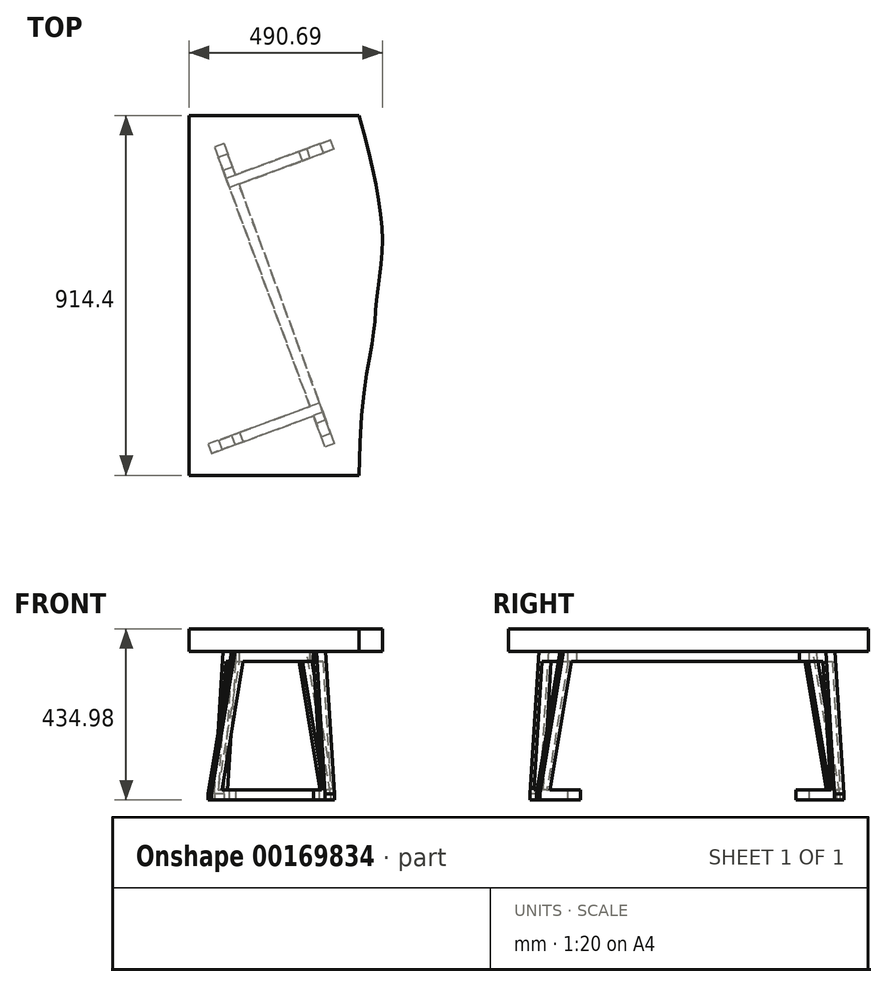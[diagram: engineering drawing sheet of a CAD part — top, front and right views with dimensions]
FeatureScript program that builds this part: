
annotation { "Feature Type Name" : "Feature", "Feature Type Description" : "" }
export const myFeature = defineFeature(function(context is Context, id is Id, definition is map)
    precondition{}
    {
        {
            var Q0;
            Q0=qCreatedBy(makeId("Top.planeOp"),FACE);
            var sketch = newSketch(context, id + "F0", { "sketchPlane" : qUnion([Q0])});
            skLineSegment(sketch, "E0", {"start": v(0, 0) * mm, "end": v(-431.8, 0) * mm});
            skLineSegment(sketch, "E1", {"start": v(-431.8, 0) * mm, "end": v(-431.8, 914.4) * mm});
            skLineSegment(sketch, "E2", {"start": v(-431.8, 914.4) * mm, "end": v(0, 914.4) * mm});
            skFitSpline(sketch, "E3", {"points": [v(0, 914.4) * mm, v(51.21, 686.94) * mm, v(57.73, 557.59) * mm, v(44.27, 444.48) * mm, v(35.04, 350.61) * mm, v(0, 0) * mm], "startDerivative": vector(304.49, -1066.3) * mm, "endDerivative": vector(0, -2055.33) * mm});
            skSolve(sketch);
        }
        {
            var Q0;
            Q0=qSketchRegion(id+"F0",true);
            extrude(context, id + "F1", {"entities" : qUnion([Q0]), "depth" : 57.15 * mm});
        }
        {
            var Q0;
            Q0=makeQuery(id+"F1.opExtrude","CAP_FACE",FACE,{"disambiguationData":[OSD([sQuery(id+"F0.wireOp",EDGE,"E0"),sQuery(id+"F0.wireOp",EDGE,"E1"),sQuery(id+"F0.wireOp",EDGE,"E2"),sQuery(id+"F0.wireOp",EDGE,"E3")])],"isStart":true});
            var sketch = newSketch(context, id + "F2", { "sketchPlane" : qUnion([Q0])});
            skLineSegment(sketch, "E4", {"start": v(-74.81, -838.2) * mm, "end": v(-355.6, -734.73) * mm});
            skLineSegment(sketch, "E5", {"start": v(-355.6, -76.2) * mm, "end": v(-74.81, -179.67) * mm});
            skLineSegment(sketch, "E6", {"start": v(-355.6, -76.2) * mm, "end": v(-355.6, -734.73) * mm});
            skLineSegment(sketch, "E7", {"start": v(-355.6, -76.2) * mm, "end": v(-355.6, 0) * mm, "construction": true});
            skLineSegment(sketch, "E8", {"start": v(-74.81, -838.2) * mm, "end": v(-74.81, -914.4) * mm, "construction": true});
            skLineSegment(sketch, "E9.bottom", {"start": v(-355.6, -76.2) * mm, "end": v(-74.81, -76.2) * mm});
            skLineSegment(sketch, "E9.top", {"start": v(-355.6, -838.2) * mm, "end": v(-74.81, -838.2) * mm});
            skLineSegment(sketch, "E9.left", {"start": v(-355.6, -76.2) * mm, "end": v(-355.6, -838.2) * mm});
            skLineSegment(sketch, "E9.right", {"start": v(-74.81, -76.2) * mm, "end": v(-74.81, -838.2) * mm});
            skLineSegment(sketch, "E10", {"start": v(-355.6, -76.2) * mm, "end": v(-431.8, -76.2) * mm, "construction": true});
            skLineSegment(sketch, "E11", {"start": v(0, 0) * mm, "end": v(0, -914.4) * mm, "construction": true});
            skLineSegment(sketch, "E12", {"start": v(-74.81, -76.2) * mm, "end": v(1.39, -76.2) * mm, "construction": true});
            skLineSegment(sketch, "E13", {"start": v(-74.81, -76.2) * mm, "end": v(-355.6, -838.2) * mm});
            skPoint(sketch, "E14", {"position": v(-108.38, -167.3) * mm});
            skPoint(sketch, "E15", {"position": v(-322.03, -747.1) * mm});
            skSolve(sketch);
        }
        {
            var Q0;
            Q0=makeQuery(id+"F1.opExtrude","SWEPT_FACE",FACE,{"disambiguationData":[OSD([sQuery(id+"F0.wireOp",EDGE,"E0")])]});
            var Q1;
            Q1=sQuery(id+"F2.wireOp",VERTEX,"E9.right.start");
            cPlane(context, id + "F3", {"entities" : qUnion([Q0, Q1]), "cplaneType" : CPlaneType.PLANE_POINT, "offset" : 25.4 * mm, "width" : 152.4 * mm, "height" : 152.4 * mm});
        }
        {
            var Q0;
            Q0=qCreatedBy(id+"F3.planeOp",FACE);
            var sketch = newSketch(context, id + "F4", { "sketchPlane" : qUnion([Q0])});
            skLineSegment(sketch, "E16", {"start": v(-74.81, 0) * mm, "end": v(-74.81, -361.95) * mm});
            skSolve(sketch);
        }
        {
            var Q0;
            Q0=sQuery(id+"F4.wireOp",VERTEX,"E16.end");
            var Q1;
            Q1=sQuery(id+"F4.wireOp",VERTEX,"E16.start");
            var Q2;
            Q2=sQuery(id+"F2.wireOp",VERTEX,"E9.left.end");
            cPlane(context, id + "F5", {"entities" : qUnion([Q0, Q1, Q2]), "cplaneType" : CPlaneType.THREE_POINT, "offset" : 25.4 * mm, "width" : 152.4 * mm, "height" : 152.4 * mm});
        }
        {
            var Q0;
            Q0=qCreatedBy(id+"F5.planeOp",FACE);
            var sketch = newSketch(context, id + "F6", { "sketchPlane" : qUnion([Q0])});
            skLineSegment(sketch, "E17", {"start": v(97.37, -361.95) * mm, "end": v(161.19, 0) * mm});
            skLineSegment(sketch, "E18", {"start": v(161.19, 0) * mm, "end": v(503.41, 0) * mm});
            skLineSegment(sketch, "E19", {"start": v(503.41, 0) * mm, "end": v(503.41, -361.95) * mm, "construction": true});
            skLineSegment(sketch, "E20", {"start": v(97.37, -361.95) * mm, "end": v(161.19, -361.95) * mm, "construction": true});
            skLineSegment(sketch, "E21", {"start": v(161.19, -361.95) * mm, "end": v(161.19, 0) * mm, "construction": true});
            skLineSegment(sketch, "E22", {"start": v(503.41, -25.4) * mm, "end": v(182.5, -25.4) * mm});
            skLineSegment(sketch, "E23", {"start": v(182.5, -25.4) * mm, "end": v(124.84, -352.43) * mm});
            skLineSegment(sketch, "E24", {"start": v(97.37, -361.95) * mm, "end": v(97.37, -377.82) * mm});
            skLineSegment(sketch, "E25", {"start": v(97.37, -377.82) * mm, "end": v(207.15, -377.82) * mm});
            skLineSegment(sketch, "E26", {"start": v(207.15, -377.82) * mm, "end": v(207.15, -352.43) * mm});
            skLineSegment(sketch, "E27", {"start": v(124.84, -352.43) * mm, "end": v(207.15, -352.43) * mm});
            skLineSegment(sketch, "E28", {"start": v(503.41, -25.4) * mm, "end": v(503.41, 0) * mm});
            skLineSegment(sketch, "E29.MirrorCS", {"start": v(503.41, -25.4) * mm, "end": v(824.32, -25.4) * mm});
            skLineSegment(sketch, "E30.MirrorCS", {"start": v(824.32, -25.4) * mm, "end": v(881.98, -352.43) * mm});
            skLineSegment(sketch, "E31.MirrorCS", {"start": v(845.63, 0) * mm, "end": v(503.41, 0) * mm});
            skLineSegment(sketch, "E32.MirrorCS", {"start": v(909.45, -361.95) * mm, "end": v(845.63, 0) * mm});
            skLineSegment(sketch, "E33.MirrorCS", {"start": v(881.98, -352.43) * mm, "end": v(799.67, -352.43) * mm});
            skLineSegment(sketch, "E34.MirrorCS", {"start": v(799.67, -377.82) * mm, "end": v(799.67, -352.43) * mm});
            skLineSegment(sketch, "E35.MirrorCS", {"start": v(909.45, -377.82) * mm, "end": v(799.67, -377.82) * mm});
            skLineSegment(sketch, "E36.MirrorCS", {"start": v(909.45, -361.95) * mm, "end": v(909.45, -377.82) * mm});
            skSolve(sketch);
        }
        {
            var Q0;
            Q0 = qSketchRegion(id + "F6", true);
            extrude(context, id + "F7", {"entities" : qUnion([Q0]), "operationType" : NewBodyOperationType.ADD, "endBound" : BoundingType.SYMMETRIC, "depth" : 25.4 * mm, "offsetDistance" : 25.4 * mm});
        }
        {
            var Q0;
            Q0=makeQuery(id+"F7.opExtrude","SWEPT_FACE",FACE,{"disambiguationData":[OSD([sQuery(id+"F6.wireOp",EDGE,"E26")])]});
            var Q1;
            Q1=sQuery(id+"F2.wireOp",VERTEX,"E14");
            cPlane(context, id + "F8", {"entities" : qUnion([Q0, Q1]), "cplaneType" : CPlaneType.PLANE_POINT, "offset" : 25.4 * mm, "width" : 152.4 * mm, "height" : 152.4 * mm});
        }
        {
            var Q0;
            Q0=qCreatedBy(id+"F8.planeOp",FACE);
            var sketch = newSketch(context, id + "F9", { "sketchPlane" : qUnion([Q0])});
            skLineSegment(sketch, "E37", {"start": v(56.55, 0) * mm, "end": v(268.57, 0) * mm});
            skLineSegment(sketch, "E38", {"start": v(268.57, 0) * mm, "end": v(332.4, -361.95) * mm});
            skLineSegment(sketch, "E39", {"start": v(332.4, -361.95) * mm, "end": v(332.4, -377.82) * mm});
            skLineSegment(sketch, "E40", {"start": v(332.4, -377.82) * mm, "end": v(56.55, -377.82) * mm});
            skLineSegment(sketch, "E41", {"start": v(56.55, -377.82) * mm, "end": v(56.55, -352.43) * mm});
            skLineSegment(sketch, "E42", {"start": v(56.55, -352.43) * mm, "end": v(304.92, -352.43) * mm});
            skLineSegment(sketch, "E43", {"start": v(304.92, -352.43) * mm, "end": v(247.26, -25.4) * mm});
            skLineSegment(sketch, "E44", {"start": v(247.26, -25.4) * mm, "end": v(56.55, -25.4) * mm});
            skLineSegment(sketch, "E45", {"start": v(56.55, -25.4) * mm, "end": v(56.55, 0) * mm});
            skLineSegment(sketch, "E46", {"start": v(388.57, 0) * mm, "end": v(388.57, -300.75) * mm, "construction": true});
            skSolve(sketch);
        }
        {
            var Q0;
            Q0 = qSketchRegion(id + "F9", true);
            extrude(context, id + "F10", {"entities" : qUnion([Q0]), "operationType" : NewBodyOperationType.ADD, "endBound" : BoundingType.SYMMETRIC, "depth" : 25.4 * mm, "offsetDistance" : 25.4 * mm});
        }
        {
            var Q0;
            Q0=makeQuery(id+"F7.opExtrude","SWEPT_FACE",FACE,{"disambiguationData":[OSD([sQuery(id+"F6.wireOp",EDGE,"E34.MirrorCS")])]});
            cPlane(context, id + "F11", {"entities" : qUnion([Q0]), "cplaneType" : CPlaneType.OFFSET, "offset" : 12.7 * mm, "oppositeDirection" : true, "width" : 152.4 * mm, "height" : 152.4 * mm});
        }
        {
            var Q0;
            Q0=qCreatedBy(id+"F11.planeOp",FACE);
            var sketch = newSketch(context, id + "F12", { "sketchPlane" : qUnion([Q0])});
            skLineSegment(sketch, "E47", {"start": v(-31.15, -377.82) * mm, "end": v(226.07, -377.82) * mm});
            skLineSegment(sketch, "E48", {"start": v(226.07, -361.95) * mm, "end": v(162.25, 0) * mm});
            skLineSegment(sketch, "E49", {"start": v(162.25, 0) * mm, "end": v(-31.15, 0) * mm});
            skLineSegment(sketch, "E50", {"start": v(-31.15, 0) * mm, "end": v(-31.15, -25.4) * mm});
            skLineSegment(sketch, "E51", {"start": v(-31.15, -25.4) * mm, "end": v(140.94, -25.4) * mm});
            skLineSegment(sketch, "E52", {"start": v(140.94, -25.4) * mm, "end": v(198.6, -352.43) * mm});
            skLineSegment(sketch, "E53", {"start": v(198.6, -352.43) * mm, "end": v(-31.15, -352.43) * mm});
            skLineSegment(sketch, "E54", {"start": v(-31.15, -352.43) * mm, "end": v(-31.15, -377.82) * mm});
            skLineSegment(sketch, "E55", {"start": v(226.07, -361.95) * mm, "end": v(226.07, -377.82) * mm});
            skSolve(sketch);
        }
        {
            var Q0;
            Q0 = qSketchRegion(id + "F12", true);
            extrude(context, id + "F13", {"entities" : qUnion([Q0]), "operationType" : NewBodyOperationType.ADD, "endBound" : BoundingType.SYMMETRIC, "depth" : 25.4 * mm, "offsetDistance" : 25.4 * mm});
        }
    });
